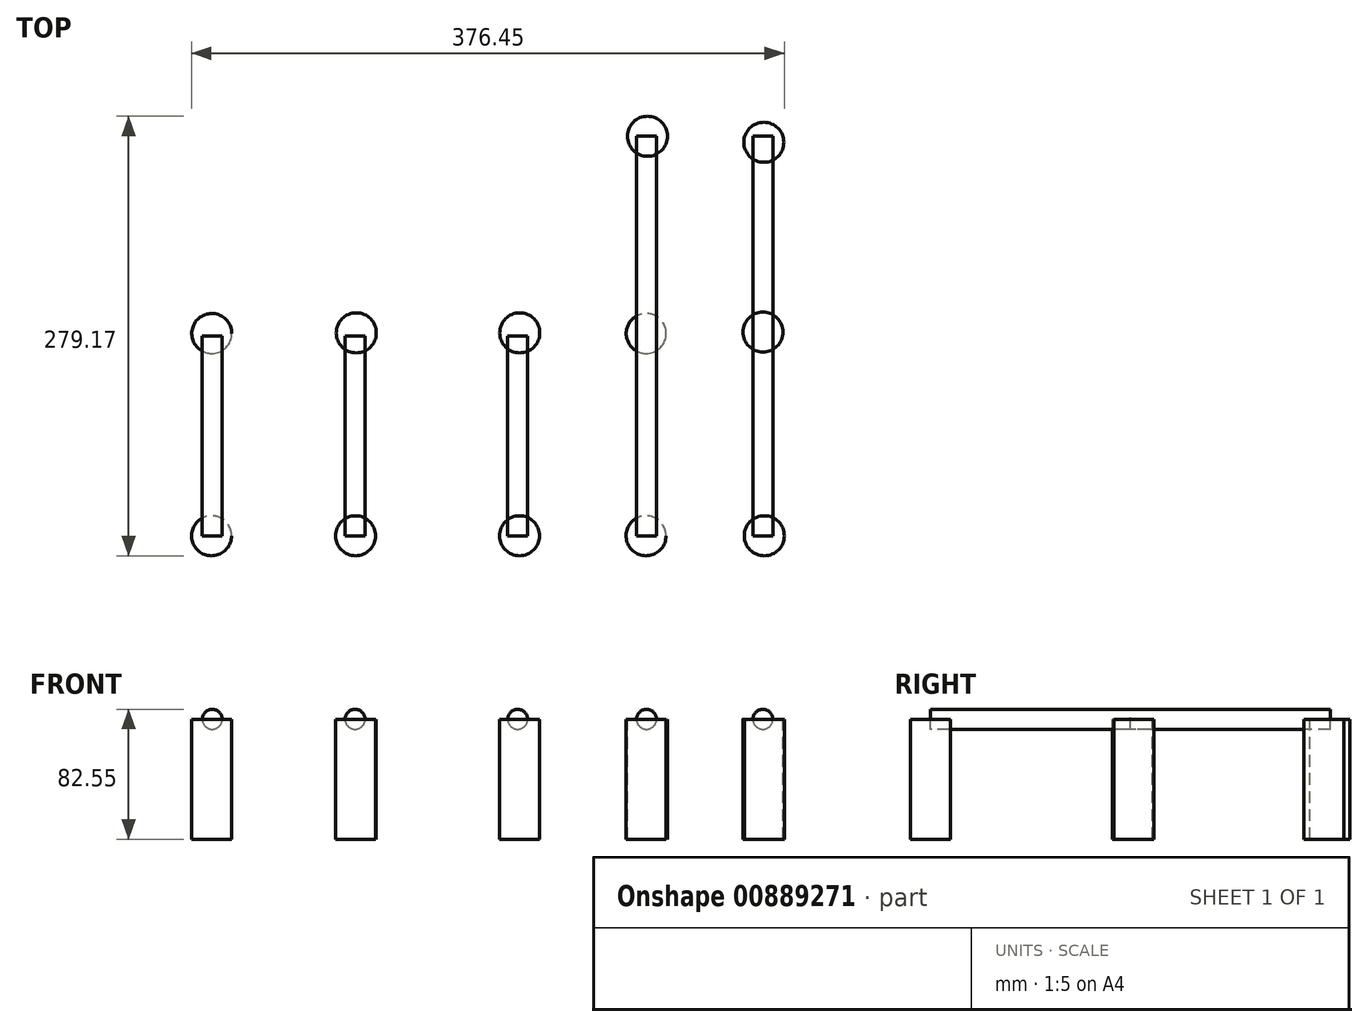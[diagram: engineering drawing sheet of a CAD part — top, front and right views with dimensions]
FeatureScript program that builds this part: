
annotation { "Feature Type Name" : "Feature", "Feature Type Description" : "" }
export const myFeature = defineFeature(function(context is Context, id is Id, definition is map)
    precondition{}
    {
        {
            var Q0;
            Q0=qCreatedBy(makeId("Front.planeOp"),FACE);
            var sketch = newSketch(context, id + "F0", { "sketchPlane" : qUnion([Q0])});
            skCircle(sketch, "E0", {"center": v(109.65, 0) * mm, "radius": 6.35 * mm});
            skCircle(sketch, "E1", {"center": v(-46.13, 0) * mm, "radius": 6.35 * mm});
            skCircle(sketch, "E2", {"center": v(35.72, 0) * mm, "radius": 6.35 * mm});
            skCircle(sketch, "E3", {"center": v(-149.36, 0) * mm, "radius": 6.35 * mm});
            skCircle(sketch, "E4", {"center": v(-240.07, 0) * mm, "radius": 6.35 * mm});
            skSolve(sketch);
        }
        {
            var Q0;
            {var subQ0=sQuery(id+"F0.wireOp",EDGE,"JXhAcLjf-cWeg-7NZL-aJu6-wowONKydlVJ1");var subQ1=sQuery(id+"F0.wireOp",EDGE,"E0");var subQ2=makeQuery(id+"F0.imprint","INTERSECT",VERTEX,{"disambiguationData":[OD(0.0)],"derivedFrom":[subQ1,subQ0]});Q0=makeQuery(id+"F0.imprint","IMPRINT",FACE,{"disambiguationData":[TD([[makeQuery(id+"F0.imprint","IMPRINT",EDGE,{"disambiguationData":[TD([[subQ2,1.0]])],"derivedFrom":subQ1}),1.0]])]});}
            var Q1;
            {var subQ0=sQuery(id+"F0.wireOp",EDGE,"JXhAcLjf-cWeg-7NZL-aJu6-wowONKydlVJ1");var subQ1=sQuery(id+"F0.wireOp",EDGE,"E2");var subQ2=makeQuery(id+"F0.imprint","INTERSECT",VERTEX,{"disambiguationData":[OD(0.0)],"derivedFrom":[subQ1,subQ0]});Q1=makeQuery(id+"F0.imprint","IMPRINT",FACE,{"disambiguationData":[TD([[makeQuery(id+"F0.imprint","IMPRINT",EDGE,{"disambiguationData":[TD([[subQ2,1.0]])],"derivedFrom":subQ1}),1.0]])]});}
            var Q2;
            Q2=qCreatedBy(makeId("Right.planeOp"),FACE);
            extrude(context, id + "F1", {"entities" : qUnion([Q0, Q1]), "oppositeDirection" : true, "depth" : 254 * mm, "endBoundEntityFace" : qUnion([Q2]), "offsetDistance" : 25.4 * mm});
        }
        {
            var Q0;
            {var subQ0=sQuery(id+"F0.wireOp",EDGE,"JXhAcLjf-cWeg-7NZL-aJu6-wowONKydlVJ1");var subQ1=sQuery(id+"F0.wireOp",EDGE,"Pitn1sYI-Vbl7-qM2A-NC5Z-sEb4D8YvEUWP");var subQ2=makeQuery(id+"F0.imprint","INTERSECT",VERTEX,{"disambiguationData":[OD(0.0)],"derivedFrom":[subQ1,subQ0]});Q0=makeQuery(id+"F0.imprint","IMPRINT",FACE,{"disambiguationData":[TD([[makeQuery(id+"F0.imprint","IMPRINT",EDGE,{"disambiguationData":[TD([[subQ2,1.0]])],"derivedFrom":subQ1}),1.0]])]});}
            var Q1;
            {var subQ0=sQuery(id+"F0.wireOp",EDGE,"JXhAcLjf-cWeg-7NZL-aJu6-wowONKydlVJ1");var subQ1=sQuery(id+"F0.wireOp",EDGE,"E1");var subQ2=makeQuery(id+"F0.imprint","INTERSECT",VERTEX,{"disambiguationData":[OD(0.0)],"derivedFrom":[subQ1,subQ0]});Q1=makeQuery(id+"F0.imprint","IMPRINT",FACE,{"disambiguationData":[TD([[makeQuery(id+"F0.imprint","IMPRINT",EDGE,{"disambiguationData":[TD([[subQ2,1.0]])],"derivedFrom":subQ1}),1.0]])]});}
            var Q2;
            {var subQ0=sQuery(id+"F0.wireOp",EDGE,"JXhAcLjf-cWeg-7NZL-aJu6-wowONKydlVJ1");var subQ1=sQuery(id+"F0.wireOp",EDGE,"je9FMlqg-uNlz-DNbJ-oCgY-3McaKznVjSO0");var subQ2=makeQuery(id+"F0.imprint","INTERSECT",VERTEX,{"disambiguationData":[OD(0.0)],"derivedFrom":[subQ1,subQ0]});Q2=makeQuery(id+"F0.imprint","IMPRINT",FACE,{"disambiguationData":[TD([[makeQuery(id+"F0.imprint","IMPRINT",EDGE,{"disambiguationData":[TD([[subQ2,1.0]])],"derivedFrom":subQ1}),1.0]])]});}
            var Q3;
            Q3=makeQuery(id+"F0.imprint","IMPRINT",FACE,{"disambiguationData":[TD([[makeQuery(id+"F0.imprint","IMPRINT",EDGE,{"derivedFrom":sQuery(id+"F0.wireOp",EDGE,"E3")}),1.0]])]});
            var Q4;
            Q4=makeQuery(id+"F0.imprint","IMPRINT",FACE,{"disambiguationData":[TD([[makeQuery(id+"F0.imprint","IMPRINT",EDGE,{"derivedFrom":sQuery(id+"F0.wireOp",EDGE,"JfNcexmA-CcbW-bNyD-IMPh-K5CZ0wvKLGR7")}),1.0]])]});
            var Q5;
            Q5=makeQuery(id+"F0.imprint","IMPRINT",FACE,{"disambiguationData":[TD([[makeQuery(id+"F0.imprint","IMPRINT",EDGE,{"derivedFrom":sQuery(id+"F0.wireOp",EDGE,"E4")}),1.0]])]});
            extrude(context, id + "F2", {"entities" : qUnion([Q0, Q1, Q2, Q3, Q4, Q5]), "oppositeDirection" : true, "depth" : 127 * mm, "offsetDistance" : 25.4 * mm});
        }
        {
            var Q0;
            Q0=qCreatedBy(makeId("Top.planeOp"),FACE);
            var sketch = newSketch(context, id + "F3", { "sketchPlane" : qUnion([Q0])});
            skLineSegment(sketch, "E5.bottom", {"start": v(-254.5, 5.53) * mm, "end": v(151.9, 5.53) * mm});
            skLineSegment(sketch, "E5.top", {"start": v(-254.5, -7.17) * mm, "end": v(151.9, -7.17) * mm});
            skLineSegment(sketch, "E6.bottom", {"start": v(-253.93, 23.3) * mm, "end": v(151.9, 23.3) * mm});
            skLineSegment(sketch, "E6.top", {"start": v(-253.93, 96.97) * mm, "end": v(151.88, 96.97) * mm});
            skLineSegment(sketch, "E7.bottom", {"start": v(-253.62, 66.49) * mm, "end": v(151.6, 66.49) * mm});
            skLineSegment(sketch, "E7.top", {"start": v(-253.93, 36) * mm, "end": v(151.6, 36) * mm});
            skLineSegment(sketch, "E8.bottom", {"start": v(-253.68, 84.27) * mm, "end": v(151.85, 84.27) * mm});
            skLineSegment(sketch, "E8.top", {"start": v(-253.93, 53.79) * mm, "end": v(151.6, 53.79) * mm});
            skLineSegment(sketch, "E9", {"start": v(-254.5, 5.53) * mm, "end": v(-254.5, -7.17) * mm});
            skLineSegment(sketch, "E10", {"start": v(151.9, 5.53) * mm, "end": v(151.9, -7.17) * mm});
            skLineSegment(sketch, "E11", {"start": v(151.9, 23.3) * mm, "end": v(151.9, 5.53) * mm});
            skLineSegment(sketch, "E12", {"start": v(-253.93, 23.3) * mm, "end": v(-254.5, 5.53) * mm});
            skLineSegment(sketch, "E13", {"start": v(-254.5, 48.72) * mm, "end": v(-254.5, 36.02) * mm});
            skLineSegment(sketch, "E14", {"start": v(151.04, 48.72) * mm, "end": v(151.04, 36.02) * mm});
            skLineSegment(sketch, "E15", {"start": v(-254.5, 36.02) * mm, "end": v(-253.93, 53.79) * mm});
            skLineSegment(sketch, "E16", {"start": v(-253.93, 53.79) * mm, "end": v(-253.93, 36) * mm});
            skLineSegment(sketch, "E17", {"start": v(-253.93, 36) * mm, "end": v(-253.93, 23.3) * mm});
            skLineSegment(sketch, "E18", {"start": v(151.6, 36) * mm, "end": v(151.9, 23.3) * mm});
            skLineSegment(sketch, "E19", {"start": v(151.6, 53.79) * mm, "end": v(151.6, 36) * mm});
            skLineSegment(sketch, "E20", {"start": v(151.6, 66.49) * mm, "end": v(151.6, 53.79) * mm});
            skLineSegment(sketch, "E21", {"start": v(151.85, 84.27) * mm, "end": v(151.6, 66.49) * mm});
            skLineSegment(sketch, "E22", {"start": v(151.88, 96.97) * mm, "end": v(151.85, 84.27) * mm});
            skLineSegment(sketch, "E23.bottom", {"start": v(-253.93, 114.74) * mm, "end": v(152.47, 114.74) * mm});
            skLineSegment(sketch, "E23.top", {"start": v(-253.89, 127.44) * mm, "end": v(152.44, 127.44) * mm});
            skLineSegment(sketch, "E24", {"start": v(152.47, 114.74) * mm, "end": v(151.88, 96.97) * mm});
            skLineSegment(sketch, "E25", {"start": v(-253.89, 127.44) * mm, "end": v(-253.93, 114.74) * mm});
            skLineSegment(sketch, "E26", {"start": v(152.44, 127.44) * mm, "end": v(152.47, 114.74) * mm});
            skLineSegment(sketch, "E27", {"start": v(-253.93, 96.97) * mm, "end": v(-253.68, 84.27) * mm});
            skLineSegment(sketch, "E28", {"start": v(-254.5, -7.17) * mm, "end": v(-254.5, 5.53) * mm});
            skLineSegment(sketch, "E29", {"start": v(-253.93, 23.3) * mm, "end": v(-253.93, 36) * mm});
            skLineSegment(sketch, "E30", {"start": v(-254.5, 53.79) * mm, "end": v(-253.62, 66.49) * mm});
            skLineSegment(sketch, "E31", {"start": v(-253.68, 84.27) * mm, "end": v(-253.62, 66.49) * mm});
            skLineSegment(sketch, "E32", {"start": v(-253.62, 66.49) * mm, "end": v(-253.93, 53.79) * mm});
            skLineSegment(sketch, "E33", {"start": v(-253.93, 114.74) * mm, "end": v(-253.93, 96.97) * mm});
            skLineSegment(sketch, "E34", {"start": v(152.44, 127.44) * mm, "end": v(152.44, 145.22) * mm});
            skLineSegment(sketch, "E35", {"start": v(152.44, 145.22) * mm, "end": v(0.04, 145.22) * mm});
            skLineSegment(sketch, "E36", {"start": v(0.04, 145.22) * mm, "end": v(0.04, 127.44) * mm});
            skLineSegment(sketch, "E37", {"start": v(0.04, 145.22) * mm, "end": v(0.04, 157.92) * mm});
            skLineSegment(sketch, "E38", {"start": v(0.04, 157.92) * mm, "end": v(152.44, 157.92) * mm});
            skLineSegment(sketch, "E39", {"start": v(152.44, 157.92) * mm, "end": v(152.44, 175.7) * mm});
            skLineSegment(sketch, "E40", {"start": v(152.44, 175.7) * mm, "end": v(0, 175.7) * mm});
            skLineSegment(sketch, "E41", {"start": v(0, 175.7) * mm, "end": v(0.04, 157.92) * mm});
            skLineSegment(sketch, "E42", {"start": v(0, 175.7) * mm, "end": v(0, 188.4) * mm});
            skLineSegment(sketch, "E43", {"start": v(0, 188.4) * mm, "end": v(152.44, 188.4) * mm});
            skLineSegment(sketch, "E44", {"start": v(152.44, 188.4) * mm, "end": v(152.44, 175.7) * mm});
            skLineSegment(sketch, "E45", {"start": v(0, 188.4) * mm, "end": v(0, 206.18) * mm});
            skLineSegment(sketch, "E46", {"start": v(0, 206.18) * mm, "end": v(152.44, 206.18) * mm});
            skLineSegment(sketch, "E47", {"start": v(152.44, 206.18) * mm, "end": v(152.44, 188.4) * mm});
            skLineSegment(sketch, "E48", {"start": v(0, 206.18) * mm, "end": v(0, 218.88) * mm});
            skLineSegment(sketch, "E49", {"start": v(0, 218.88) * mm, "end": v(152.44, 218.88) * mm});
            skLineSegment(sketch, "E50", {"start": v(152.44, 218.88) * mm, "end": v(152.44, 206.18) * mm});
            skLineSegment(sketch, "E51", {"start": v(0, 218.88) * mm, "end": v(0, 236.66) * mm});
            skLineSegment(sketch, "E52", {"start": v(0, 236.66) * mm, "end": v(152.44, 236.66) * mm});
            skLineSegment(sketch, "E53", {"start": v(152.44, 236.66) * mm, "end": v(152.44, 218.88) * mm});
            skLineSegment(sketch, "E54", {"start": v(0, 236.66) * mm, "end": v(0, 249.36) * mm});
            skLineSegment(sketch, "E55", {"start": v(0, 249.36) * mm, "end": v(152.44, 249.36) * mm});
            skLineSegment(sketch, "E56", {"start": v(152.44, 249.36) * mm, "end": v(152.44, 236.66) * mm});
            skLineSegment(sketch, "E57", {"start": v(152.44, 145.22) * mm, "end": v(152.44, 157.92) * mm});
            skSolve(sketch);
        }
        {
            var Q0;
            Q0=sQuery(id+"F3.wireOp",EDGE,"E5.top");
            var Q1;
            Q1=sQuery(id+"F3.wireOp",EDGE,"E5.bottom");
            var Q2;
            Q2=sQuery(id+"F3.wireOp",EDGE,"E6.bottom");
            var Q3;
            Q3=sQuery(id+"F3.wireOp",EDGE,"E7.top");
            var Q4;
            Q4=sQuery(id+"F3.wireOp",EDGE,"E9");
            var Q5;
            Q5=sQuery(id+"F3.wireOp",EDGE,"E17");
            var Q6;
            Q6=sQuery(id+"F3.wireOp",EDGE,"E25");
            var Q7;
            Q7=sQuery(id+"F3.wireOp",EDGE,"E23.bottom");
            var Q8;
            Q8=sQuery(id+"F3.wireOp",EDGE,"E23.top");
            var Q9;
            Q9=sQuery(id+"F3.wireOp",EDGE,"E6.top");
            var Q10;
            Q10=sQuery(id+"F3.wireOp",EDGE,"E8.bottom");
            var Q11;
            Q11=sQuery(id+"F3.wireOp",EDGE,"E22");
            var Q12;
            Q12=sQuery(id+"F3.wireOp",EDGE,"E7.bottom");
            var Q13;
            Q13=sQuery(id+"F3.wireOp",EDGE,"E8.top");
            var Q14;
            Q14=sQuery(id+"F3.wireOp",EDGE,"E20");
            var Q15;
            Q15=sQuery(id+"F3.wireOp",EDGE,"E10");
            var Q16;
            Q16=sQuery(id+"F3.wireOp",EDGE,"E18");
            var Q17;
            Q17=sQuery(id+"F3.wireOp",EDGE,"E26");
            var Q18;
            Q18=sQuery(id+"F3.wireOp",EDGE,"E54");
            var Q19;
            Q19=sQuery(id+"F3.wireOp",EDGE,"E56");
            var Q20;
            Q20=sQuery(id+"F3.wireOp",EDGE,"E55");
            var Q21;
            Q21=sQuery(id+"F3.wireOp",EDGE,"E52");
            var Q22;
            Q22=sQuery(id+"F3.wireOp",EDGE,"E48");
            var Q23;
            Q23=sQuery(id+"F3.wireOp",EDGE,"E50");
            var Q24;
            Q24=sQuery(id+"F3.wireOp",EDGE,"E49");
            var Q25;
            Q25=sQuery(id+"F3.wireOp",EDGE,"E46");
            var Q26;
            Q26=sQuery(id+"F3.wireOp",EDGE,"E42");
            var Q27;
            Q27=sQuery(id+"F3.wireOp",EDGE,"E44");
            var Q28;
            Q28=sQuery(id+"F3.wireOp",EDGE,"E43");
            var Q29;
            Q29=sQuery(id+"F3.wireOp",EDGE,"E40");
            var Q30;
            Q30=sQuery(id+"F3.wireOp",EDGE,"E35");
            var Q31;
            Q31=sQuery(id+"F3.wireOp",EDGE,"E37");
            var Q32;
            Q32=sQuery(id+"F3.wireOp",EDGE,"E27");
            var Q33;
            Q33=sQuery(id+"F3.wireOp",EDGE,"E32");
            var Q34;
            Q34=sQuery(id+"F3.wireOp",EDGE,"E38");
            var Q35;
            Q35=sQuery(id+"F3.wireOp",EDGE,"E57");
            extrude(context, id + "F4", {"bodyType" : ToolBodyType.SURFACE, "surfaceEntities" : qUnion([Q0, Q1, Q2, Q3, Q4, Q5, Q6, Q7, Q8, Q9, Q10, Q11, Q12, Q13, Q14, Q15, Q16, Q17, Q18, Q19, Q20, Q21, Q22, Q23, Q24, Q25, Q26, Q27, Q28, Q29, Q30, Q31, Q32, Q33, Q34, Q35]), "depth" : 12.7 * mm, "offsetDistance" : 25.4 * mm, "hasSecondDirection" : true, "secondDirectionOppositeDirection" : true, "secondDirectionDepth" : 25.4 * mm});
        }
        {
            var Q0;
            Q0=qCreatedBy(makeId("Top.planeOp"),FACE);
            var sketch = newSketch(context, id + "F5", { "sketchPlane" : qUnion([Q0])});
            skCircle(sketch, "E58", {"center": v(-240.48, 0) * mm, "radius": 12.7 * mm});
            skCircle(sketch, "E59", {"center": v(-240.35, 128.5) * mm, "radius": 12.7 * mm});
            skCircle(sketch, "E60", {"center": v(-148.58, 128.88) * mm, "radius": 12.7 * mm});
            skCircle(sketch, "E61", {"center": v(-149.04, 0) * mm, "radius": 12.7 * mm});
            skCircle(sketch, "E62", {"center": v(-44.9, 0) * mm, "radius": 12.7 * mm});
            skCircle(sketch, "E63", {"center": v(-44.78, 128.88) * mm, "radius": 12.7 * mm});
            skCircle(sketch, "E64", {"center": v(35.45, 0) * mm, "radius": 12.7 * mm});
            skCircle(sketch, "E65", {"center": v(36.34, 253.77) * mm, "radius": 12.7 * mm});
            skCircle(sketch, "E66", {"center": v(110.26, 249.94) * mm, "radius": 12.7 * mm});
            skCircle(sketch, "E67", {"center": v(35.54, 128.5) * mm, "radius": 12.7 * mm});
            skCircle(sketch, "E68", {"center": v(109.71, 129.37) * mm, "radius": 12.7 * mm});
            skCircle(sketch, "E69", {"center": v(110.57, 0) * mm, "radius": 12.7 * mm});
            skSolve(sketch);
        }
        {
            var Q0;
            Q0=makeQuery(id+"F5.imprint","IMPRINT",FACE,{"disambiguationData":[TD([[makeQuery(id+"F5.imprint","IMPRINT",EDGE,{"derivedFrom":sQuery(id+"F5.wireOp",EDGE,"E58")}),1.0]])]});
            var Q1;
            Q1=makeQuery(id+"F5.imprint","IMPRINT",FACE,{"disambiguationData":[TD([[makeQuery(id+"F5.imprint","IMPRINT",EDGE,{"derivedFrom":sQuery(id+"F5.wireOp",EDGE,"E59")}),1.0]])]});
            var Q2;
            Q2=makeQuery(id+"F5.imprint","IMPRINT",FACE,{"disambiguationData":[TD([[makeQuery(id+"F5.imprint","IMPRINT",EDGE,{"derivedFrom":sQuery(id+"F5.wireOp",EDGE,"E60")}),1.0]])]});
            var Q3;
            Q3=makeQuery(id+"F5.imprint","IMPRINT",FACE,{"disambiguationData":[TD([[makeQuery(id+"F5.imprint","IMPRINT",EDGE,{"derivedFrom":sQuery(id+"F5.wireOp",EDGE,"E61")}),1.0]])]});
            var Q4;
            Q4=makeQuery(id+"F5.imprint","IMPRINT",FACE,{"disambiguationData":[TD([[makeQuery(id+"F5.imprint","IMPRINT",EDGE,{"derivedFrom":sQuery(id+"F5.wireOp",EDGE,"E62")}),1.0]])]});
            var Q5;
            Q5=makeQuery(id+"F5.imprint","IMPRINT",FACE,{"disambiguationData":[TD([[makeQuery(id+"F5.imprint","IMPRINT",EDGE,{"derivedFrom":sQuery(id+"F5.wireOp",EDGE,"E63")}),1.0]])]});
            var Q6;
            Q6=makeQuery(id+"F5.imprint","IMPRINT",FACE,{"disambiguationData":[TD([[makeQuery(id+"F5.imprint","IMPRINT",EDGE,{"derivedFrom":sQuery(id+"F5.wireOp",EDGE,"E64")}),1.0]])]});
            var Q7;
            Q7=makeQuery(id+"F5.imprint","IMPRINT",FACE,{"disambiguationData":[TD([[makeQuery(id+"F5.imprint","IMPRINT",EDGE,{"derivedFrom":sQuery(id+"F5.wireOp",EDGE,"E69")}),1.0]])]});
            var Q8;
            Q8=makeQuery(id+"F5.imprint","IMPRINT",FACE,{"disambiguationData":[TD([[makeQuery(id+"F5.imprint","IMPRINT",EDGE,{"derivedFrom":sQuery(id+"F5.wireOp",EDGE,"E68")}),1.0]])]});
            var Q9;
            Q9=makeQuery(id+"F5.imprint","IMPRINT",FACE,{"disambiguationData":[TD([[makeQuery(id+"F5.imprint","IMPRINT",EDGE,{"derivedFrom":sQuery(id+"F5.wireOp",EDGE,"E65")}),1.0]])]});
            var Q10;
            Q10=makeQuery(id+"F5.imprint","IMPRINT",FACE,{"disambiguationData":[TD([[makeQuery(id+"F5.imprint","IMPRINT",EDGE,{"derivedFrom":sQuery(id+"F5.wireOp",EDGE,"E66")}),1.0]])]});
            var Q11;
            Q11=makeQuery(id+"F5.imprint","IMPRINT",FACE,{"disambiguationData":[TD([[makeQuery(id+"F5.imprint","IMPRINT",EDGE,{"derivedFrom":sQuery(id+"F5.wireOp",EDGE,"E67")}),1.0]])]});
            extrude(context, id + "F6", {"entities" : qUnion([Q0, Q1, Q2, Q3, Q4, Q5, Q6, Q7, Q8, Q9, Q10, Q11]), "oppositeDirection" : true, "depth" : 76.2 * mm, "offsetDistance" : 25.4 * mm});
        }
    });
